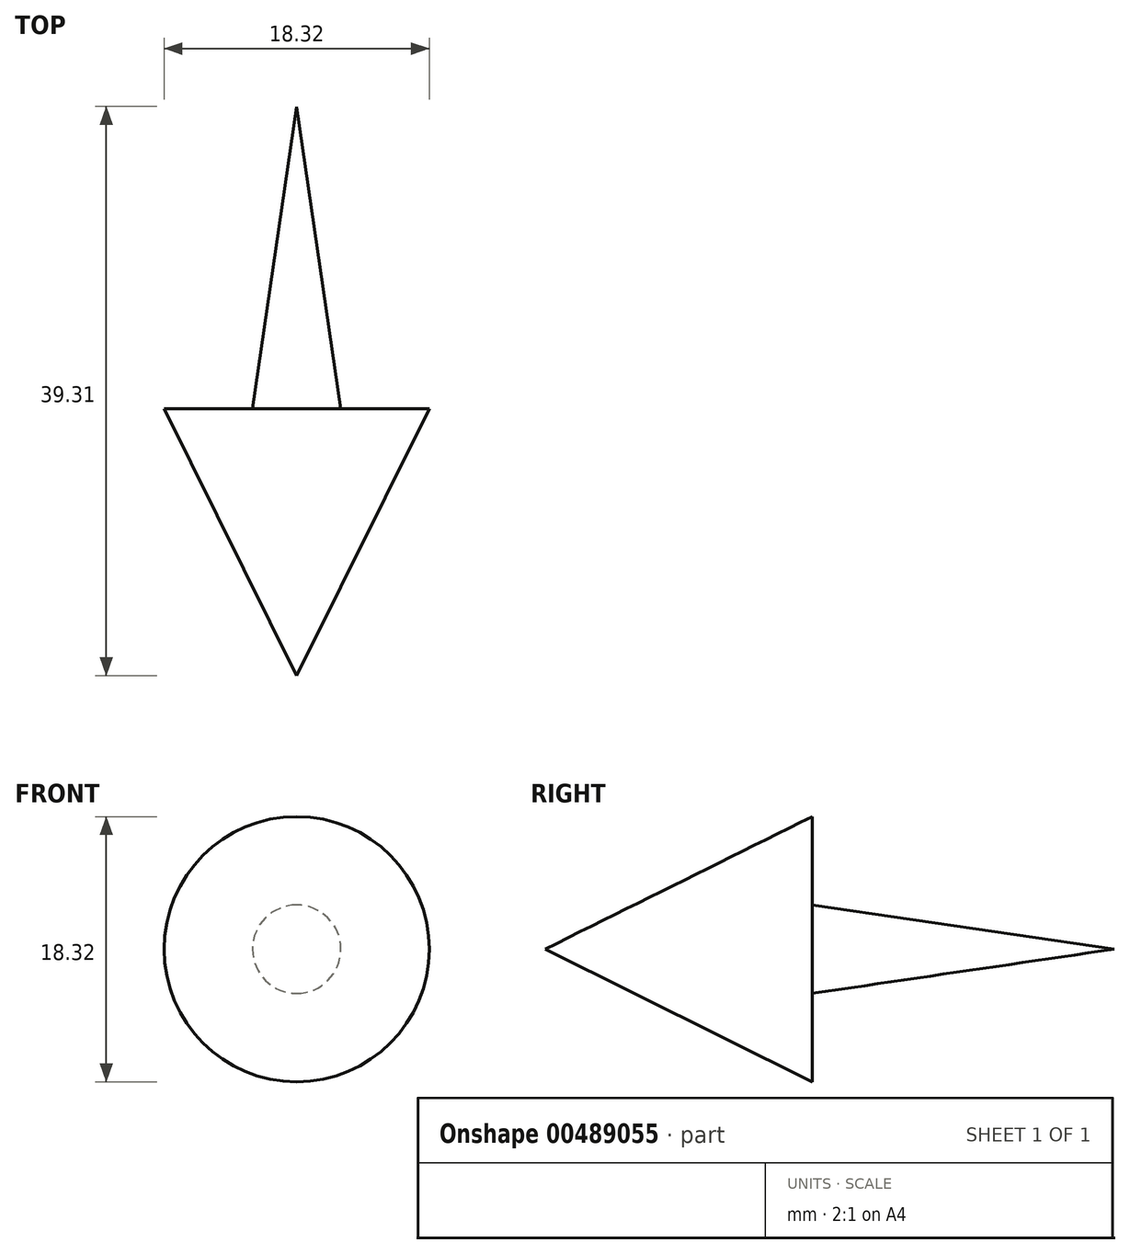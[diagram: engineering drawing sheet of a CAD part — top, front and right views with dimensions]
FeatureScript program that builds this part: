
annotation { "Feature Type Name" : "Feature", "Feature Type Description" : "" }
export const myFeature = defineFeature(function(context is Context, id is Id, definition is map)
    precondition{}
    {
        {
            var Q0;
            Q0=qCreatedBy(makeId("Top.planeOp"),FACE);
            var sketch = newSketch(context, id + "F0", { "sketchPlane" : qUnion([Q0])});
            skLineSegment(sketch, "E0", {"start": v(0, 39.3) * mm, "end": v(0, 0) * mm});
            skLineSegment(sketch, "E1", {"start": v(0, 39.3) * mm, "end": v(-3.05, 18.44) * mm});
            skLineSegment(sketch, "E2", {"start": v(-3.05, 18.44) * mm, "end": v(-9.16, 18.44) * mm});
            skLineSegment(sketch, "E3", {"start": v(-9.16, 18.44) * mm, "end": v(0, 0) * mm});
            skSolve(sketch);
        }
        {
            var Q0;
            Q0=makeQuery(id+"F0.imprint","IMPRINT",FACE,{"disambiguationData":[TD([[makeQuery(id+"F0.imprint","IMPRINT",EDGE,{"derivedFrom":sQuery(id+"F0.wireOp",EDGE,"E0")}),-1.0]])]});
            var Q1;
            Q1=sQuery(id+"F0.wireOp",EDGE,"E0");
            revolve(context, id + "F1", {"entities" : qUnion([Q0]), "axis" : qUnion([Q1]), "revolveType" : RevolveType.FULL});
        }
    });
